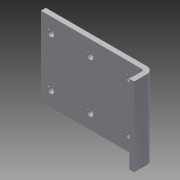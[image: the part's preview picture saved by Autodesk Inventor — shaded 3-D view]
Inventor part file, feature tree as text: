
AUTODESK INVENTOR PART (.ipt)
format: ipt  version: 2014 (Build 180170000, 170)  size: 110,080 bytes
history: native  units: in
note: dims shown in document units (in); Inventor stores cm internally (conversion verified against a paired STEP export)
features: sheet_metal_op x4, sketch x2, other x2
ambient origin geometry x8: Origin, YZ Plane, XZ Plane, XY Plane, X Axis, Y Axis, Z Axis, Center Point
bodies: Solid1 (feature_tree)
feature tree (8):
  sheet_metal_op  "Face1"
  sheet_metal_op  "Flange1"
  sketch  "Sketch1"  dims[d1=1.1811in d3=0.7874in d4=2.0in d5=2.75in d6=0.163in d7=0.25in d8=0.375in d9=1.0in d10=1.25in]
  other  "Plate1"
  sketch  "Sketch2"  dims[d11=0.125in d12=0.125in d13=0.0625in d14=0.25in d15=0.125in d16=0.5in d17=90.0deg d18=0.05in d19=0.5in d20=0.125in d21=0.125in]
  other  "Plate2"
  sheet_metal_op  "Bend1"
  sheet_metal_op  "Corner1"
